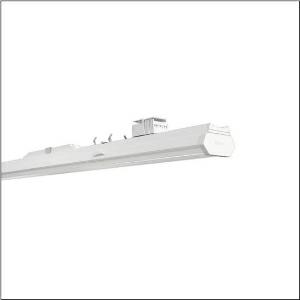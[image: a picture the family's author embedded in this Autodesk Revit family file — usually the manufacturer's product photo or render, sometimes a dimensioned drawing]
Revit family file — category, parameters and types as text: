
# Revit family: licross_11_protected_ho_51tp12dn4fxm3c
name_source: partatom
category: Lighting Fixtures
units: mm (PartAtom-declared; Revit-internal decimal feet)

## family parameters
Cut with Voids When Loaded = No
Host = Face
Light Source = No
Part Type = Normal
Room Calculation Point = No
Round Connector Dimension = Use Diameter
Shared = No

## types (1)
- --- (1 x LED, 970 lm, 7.4 W, 4000K)
    Apparent Load = 7 VA
    CIE Flux Codes = 70 91 97 98 100
    Color Rendering = 80
    Color Temperature = 4000K
    Default Elevation = 1800 mm
    Description = Licross 11 Protected HO, luminaire insert, of sheet steel, galvanised, coil coated, white, length: 1.500mm, width: 90mm, height: 101mm, LED rated luminous flux: 15.270lm, light colour: 840, SDCM (Standard Deviation of Colour Matching)MacAdam ≤ 2 SDCM (initial), control gear: DALI 2 (for two DALI lines), with plug, 6-pole, with phase selection, for trunking rail, 14-core, mains connection: 220..240V, AC, 50/60Hz, rated input power: 91W, for trunking rail, 14-core, internal wiring halogen-free, for emergency light function, converter,control gear: single battery element, battery: LiFePO4, 9Ah, primary light control with lens, of plastic, primary optical cover: cover, of PMMA, light emission: direct distribution, primary light characteristic: symmetric, protection rating (complete): IP64, insulation class (complete): insulation class I (protective earthing), certification: CE, UKCA, protection symbol: D if used in an environment with conductive dust loads with corresponding accessories, impact resistance: IK06, permissible ambient temperature for indoor applications: +5..+30°C, standard: EN 60598-2-22, LABS conformity tested according to VDMA 24364:2018-05, reducing of maximum allowable ambient temperature of 5°C with ceiling mounting, corresponds to IFS (International Featured Standards) requirements for safety and quality in the food industry, The light source and the operating device comply with the requirements of the Ecodesign Regulation (EU) 2019/2020 and are replaceable in accordance with this regulation, packaging unit: 1 piece
    Height = 92 mm
    Lamp = 1 x LED
    Lamp Light Flux = 970 lm
    Lamp Power = 7.4 W
    Lamp count = 1
    Length = 1500 mm
    Luminous efficacy = 131 lm/W
    Manufacturer = Siteco
    ModVariant = No
    Model = 51TP12DN4FXM3C
    Mounting Place = Ceiling
    Mounting Type = Pendant
    Number of Poles = 1
    OnlyDefault = Yes
    Power Factor = 1
    Product Name = Licross 11 Protected HO
    Product group = luminaire insert | ceiling pendant
    ProductGroupID = 901
    Protection Class = Protection class I
    Protection Degree = IP 64
    RLX_Detail_Level = 1
    RLX_Emergency_Light_Flux = 0 lm
    RLX_Emergency_Type = 0
    RLX_Emergency_Type_DB = No
    RlxData = <blob elided: 25161 chars, md5=6867533c>
    Socket = socket
    Standby Power = 0 W
    System Light Flux = 970 lm
    System Power = 7 W
    Type Comments = : emergency light operation: 3 h
    Type Image = l_1256148.jpg
    URL = http://relux.com
    VarID = @adj_094787
    Voltage = 0 V
    Weight = 0.00 kg
    Width = 88 mm

## geometry (parser evidence)
native form markers: Blend x4, Sweep x9
no freeform markers — native parametric forms only
